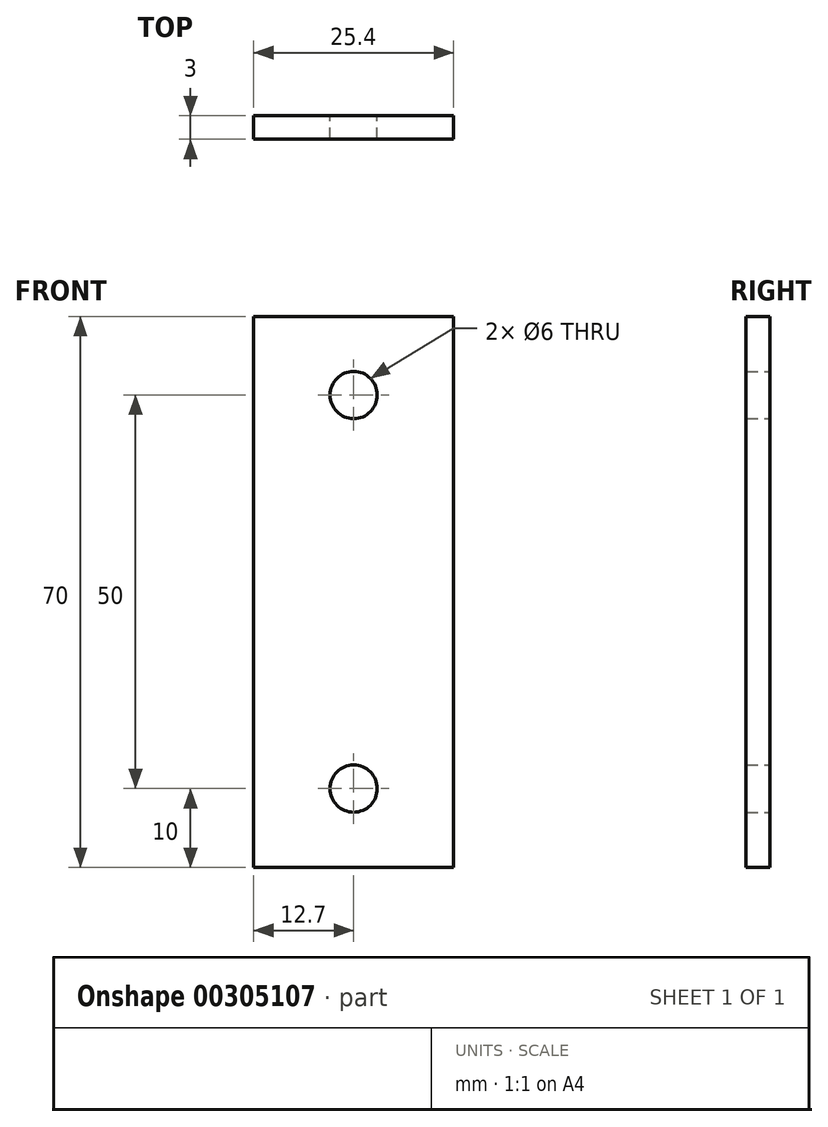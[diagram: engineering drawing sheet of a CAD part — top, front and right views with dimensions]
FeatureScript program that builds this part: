
annotation { "Feature Type Name" : "Feature", "Feature Type Description" : "" }
export const myFeature = defineFeature(function(context is Context, id is Id, definition is map)
    precondition{}
    {
        {
            var Q0;
            Q0=qCreatedBy(makeId("Front.planeOp"),FACE);
            var sketch = newSketch(context, id + "F0", { "sketchPlane" : qUnion([Q0])});
            skLineSegment(sketch, "E0.bottom", {"start": v(12.7, -35) * mm, "end": v(-12.7, -35) * mm});
            skLineSegment(sketch, "E0.top", {"start": v(12.7, 35) * mm, "end": v(-12.7, 35) * mm});
            skLineSegment(sketch, "E0.left", {"start": v(12.7, -35) * mm, "end": v(12.7, 35) * mm});
            skLineSegment(sketch, "E0.right", {"start": v(-12.7, -35) * mm, "end": v(-12.7, 35) * mm});
            skPoint(sketch, "E0.middle", {"position": v(0, 0) * mm});
            skLineSegment(sketch, "E1", {"start": v(0, 25) * mm, "end": v(0, -25) * mm});
            skCircle(sketch, "E2", {"center": v(0, 25) * mm, "radius": 3 * mm});
            skCircle(sketch, "E3", {"center": v(0, -25) * mm, "radius": 3 * mm});
            skSolve(sketch);
        }
        {
            var Q0;
            Q0=makeQuery(id+"F0.imprint","IMPRINT",FACE,{"disambiguationData":[TD([[makeQuery(id+"F0.imprint","IMPRINT",EDGE,{"derivedFrom":sQuery(id+"F0.wireOp",EDGE,"E0.bottom")}),-1.0]])]});
            extrude(context, id + "F1", {"entities" : qUnion([Q0]), "depth" : 3 * mm});
        }
    });
